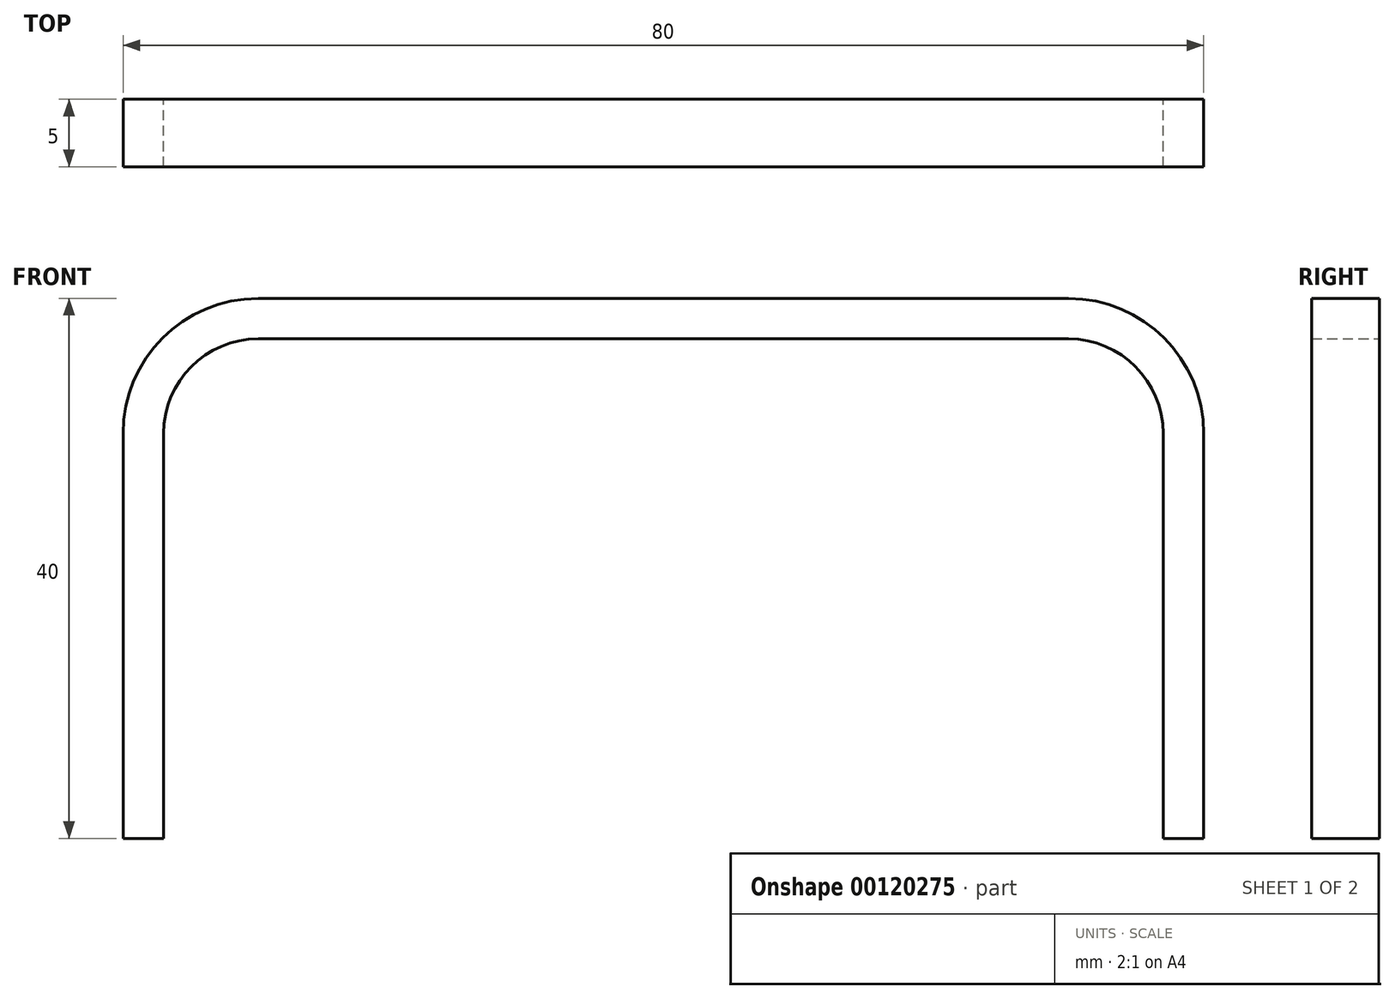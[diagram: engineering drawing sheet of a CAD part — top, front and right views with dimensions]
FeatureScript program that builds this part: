
annotation { "Feature Type Name" : "Feature", "Feature Type Description" : "" }
export const myFeature = defineFeature(function(context is Context, id is Id, definition is map)
    precondition{}
    {
        {
            var Q0;
            Q0=qCreatedBy(makeId("Front.planeOp"),FACE);
            var sketch = newSketch(context, id + "F0", { "sketchPlane" : qUnion([Q0])});
            skLineSegment(sketch, "E0.bottom", {"start": v(-40, 0) * mm, "end": v(40, 0) * mm});
            skLineSegment(sketch, "E0.top", {"start": v(-30, 40) * mm, "end": v(30, 40) * mm});
            skLineSegment(sketch, "E0.left", {"start": v(-40, 0) * mm, "end": v(-40, 30) * mm});
            skLineSegment(sketch, "E0.right", {"start": v(40, 0) * mm, "end": v(40, 30) * mm});
            skPoint(sketch, "E1.visualSharp", {"position": v(-40, 40) * mm});
            skArc(sketch, "E1.filletArc", {"start": v(-30, 40) * mm, "mid": v(-37.07, 37.07) * mm, "end": v(-40, 30) * mm});
            skPoint(sketch, "E2.visualSharp", {"position": v(40, 40) * mm});
            skArc(sketch, "E2.filletArc", {"start": v(40, 30) * mm, "mid": v(37.07, 37.07) * mm, "end": v(30, 40) * mm});
            skLineSegment(sketch, "E3.0", {"start": v(-37, 0) * mm, "end": v(-37, 30) * mm});
            skLineSegment(sketch, "E3.1", {"start": v(37, 0) * mm, "end": v(37, 30) * mm});
            skArc(sketch, "E3.2", {"start": v(37, 30) * mm, "mid": v(34.95, 34.95) * mm, "end": v(30, 37) * mm});
            skLineSegment(sketch, "E3.3", {"start": v(-30, 37) * mm, "end": v(30, 37) * mm});
            skArc(sketch, "E3.4", {"start": v(-30, 37) * mm, "mid": v(-34.95, 34.95) * mm, "end": v(-37, 30) * mm});
            skSolve(sketch);
        }
        {
            var Q0;
            Q0=makeQuery(id+"F0.imprint","IMPRINT",FACE,{"disambiguationData":[TD([[makeQuery(id+"F0.imprint","IMPRINT",EDGE,{"derivedFrom":sQuery(id+"F0.wireOp",EDGE,"E0.top")}),-1.0]])]});
            extrude(context, id + "F1", {"entities" : qUnion([Q0]), "depth" : 5 * mm});
        }
    });
